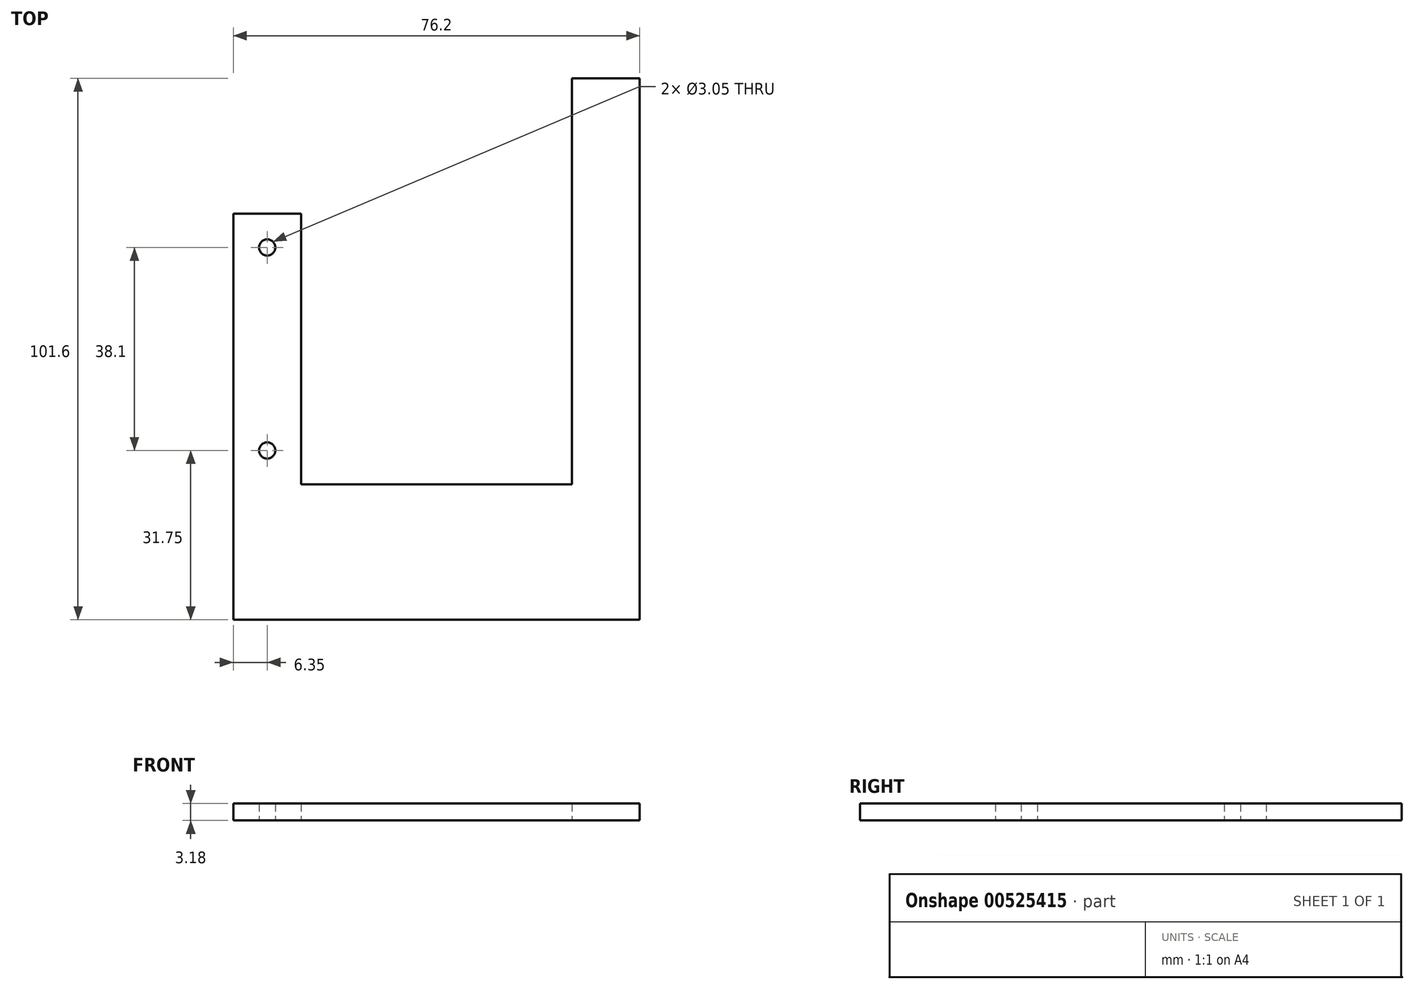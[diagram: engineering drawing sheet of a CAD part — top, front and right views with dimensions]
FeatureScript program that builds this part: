
annotation { "Feature Type Name" : "Feature", "Feature Type Description" : "" }
export const myFeature = defineFeature(function(context is Context, id is Id, definition is map)
    precondition{}
    {
        {
            var Q0;
            Q0=qCreatedBy(makeId("Top.planeOp"),FACE);
            var sketch = newSketch(context, id + "F0", { "sketchPlane" : qUnion([Q0])});
            skLineSegment(sketch, "E0.bottom", {"start": v(25.4, 12.7) * mm, "end": v(-25.4, 12.7) * mm});
            skLineSegment(sketch, "E0.top", {"start": v(25.4, -12.7) * mm, "end": v(-25.4, -12.7) * mm});
            skLineSegment(sketch, "E0.left", {"start": v(25.4, 12.7) * mm, "end": v(25.4, -12.7) * mm});
            skLineSegment(sketch, "E0.right", {"start": v(-25.4, 12.7) * mm, "end": v(-25.4, -12.7) * mm});
            skPoint(sketch, "E0.middle", {"position": v(0, 0) * mm});
            skLineSegment(sketch, "E1.bottom", {"start": v(-25.4, -12.7) * mm, "end": v(-38.1, -12.7) * mm});
            skLineSegment(sketch, "E1.top", {"start": v(-25.4, 63.5) * mm, "end": v(-38.1, 63.5) * mm});
            skLineSegment(sketch, "E1.left", {"start": v(-25.4, -12.7) * mm, "end": v(-25.4, 63.5) * mm});
            skLineSegment(sketch, "E1.right", {"start": v(-38.1, -12.7) * mm, "end": v(-38.1, 63.5) * mm});
            skLineSegment(sketch, "E2.bottom", {"start": v(25.4, -12.7) * mm, "end": v(38.1, -12.7) * mm});
            skLineSegment(sketch, "E2.top", {"start": v(25.4, 88.9) * mm, "end": v(38.1, 88.9) * mm});
            skLineSegment(sketch, "E2.left", {"start": v(25.4, -12.7) * mm, "end": v(25.4, 88.9) * mm});
            skLineSegment(sketch, "E2.right", {"start": v(38.1, -12.7) * mm, "end": v(38.1, 88.9) * mm});
            skCircle(sketch, "E3", {"center": v(-31.75, 19.05) * mm, "radius": 1.52 * mm});
            skPoint(sketch, "E3.centerSnap0", {"position": v(-31.75, -12.7) * mm});
            skCircle(sketch, "E4", {"center": v(-31.75, 57.15) * mm, "radius": 1.52 * mm});
            skSolve(sketch);
        }
        {
            var Q0;
            {var subQ0=sQuery(id+"F0.wireOp",EDGE,"E0.bottom");Q0=makeQuery(id+"F0.imprint","IMPRINT",FACE,{"disambiguationData":[TD([[makeQuery(id+"F0.imprint","IMPRINT",EDGE,{"derivedFrom":subQ0}),1.0]])]});}
            var Q1;
            {var subQ3=sQuery(id+"F0.wireOp",EDGE,"E1.bottom");Q1=makeQuery(id+"F0.imprint","IMPRINT",FACE,{"disambiguationData":[TD([[makeQuery(id+"F0.imprint","IMPRINT",EDGE,{"derivedFrom":subQ3}),-1.0]])]});}
            var Q2;
            {var subQ3=sQuery(id+"F0.wireOp",EDGE,"E2.bottom");Q2=makeQuery(id+"F0.imprint","IMPRINT",FACE,{"disambiguationData":[TD([[makeQuery(id+"F0.imprint","IMPRINT",EDGE,{"derivedFrom":subQ3}),1.0]])]});}
            extrude(context, id + "F1", {"entities" : qUnion([Q0, Q1, Q2]), "depth" : 3.17 * mm, "offsetDistance" : 25.4 * mm});
        }
    });
